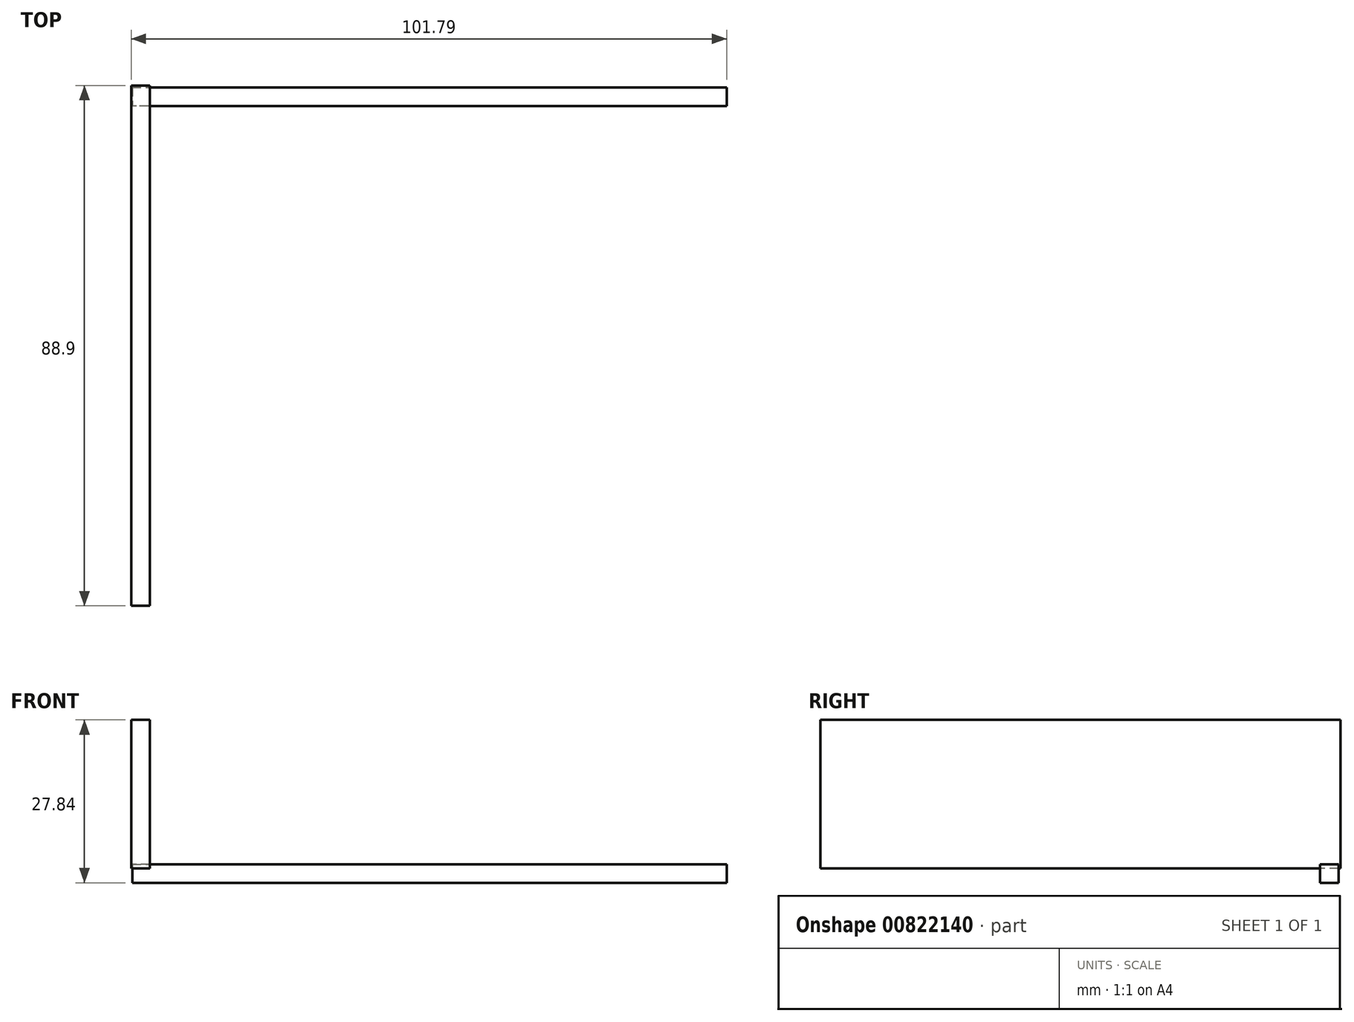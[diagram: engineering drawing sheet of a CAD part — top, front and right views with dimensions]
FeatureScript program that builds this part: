
annotation { "Feature Type Name" : "Feature", "Feature Type Description" : "" }
export const myFeature = defineFeature(function(context is Context, id is Id, definition is map)
    precondition{}
    {
        {
            var Q0;
            Q0=qCreatedBy(makeId("Top.planeOp"),FACE);
            var sketch = newSketch(context, id + "F0", { "sketchPlane" : qUnion([Q0])});
            skLineSegment(sketch, "E0", {"start": v(-47.87, 88.58) * mm, "end": v(53.73, 88.58) * mm});
            skLineSegment(sketch, "E1", {"start": v(-47.87, 88.58) * mm, "end": v(-47.87, -76.52) * mm});
            skLineSegment(sketch, "E2", {"start": v(53.73, 88.58) * mm, "end": v(53.73, -76.52) * mm});
            skArc(sketch, "E3", {"start": v(53.73, -76.52) * mm, "mid": v(2.93, -50.7) * mm, "end": v(-47.87, -76.52) * mm});
            skLineSegment(sketch, "E4", {"start": v(53.73, 85.4) * mm, "end": v(53.73, 88.58) * mm});
            skLineSegment(sketch, "E5", {"start": v(53.73, 85.4) * mm, "end": v(-47.87, 85.4) * mm});
            skLineSegment(sketch, "E6", {"start": v(-47.87, 85.4) * mm, "end": v(-47.87, 88.58) * mm});
            skSolve(sketch);
        }
        {
            var Q0;
            Q0=makeQuery(id+"F0.imprint","IMPRINT",FACE,{"disambiguationData":[TD([[makeQuery(id+"F0.imprint","IMPRINT",EDGE,{"derivedFrom":sQuery(id+"F0.wireOp",EDGE,"E0")}),-1.0]])]});
            extrude(context, id + "F1", {"entities" : qUnion([Q0]), "depth" : 3.17 * mm, "offsetDistance" : 25.4 * mm});
        }
        {
            var Q0;
            Q0=qCreatedBy(makeId("Front.planeOp"),FACE);
            var sketch = newSketch(context, id + "F2", { "sketchPlane" : qUnion([Q0])});
            skLineSegment(sketch, "E7", {"start": v(-48.06, 2.44) * mm, "end": v(-48.06, 27.84) * mm});
            skLineSegment(sketch, "E8", {"start": v(-48.06, 27.84) * mm, "end": v(-44.88, 27.84) * mm});
            skLineSegment(sketch, "E9", {"start": v(-44.88, 27.84) * mm, "end": v(-44.88, 2.44) * mm});
            skLineSegment(sketch, "E10", {"start": v(-48.06, 2.44) * mm, "end": v(-44.88, 2.44) * mm});
            skSolve(sketch);
        }
        {
            var Q0;
            Q0=makeQuery(id+"F2.imprint","IMPRINT",FACE,{"disambiguationData":[TD([[makeQuery(id+"F2.imprint","IMPRINT",EDGE,{"derivedFrom":sQuery(id+"F2.wireOp",EDGE,"E7")}),-1.0]])]});
            extrude(context, id + "F3", {"entities" : qUnion([Q0]), "oppositeDirection" : true, "depth" : 88.9 * mm, "offsetDistance" : 25.4 * mm});
        }
    });
